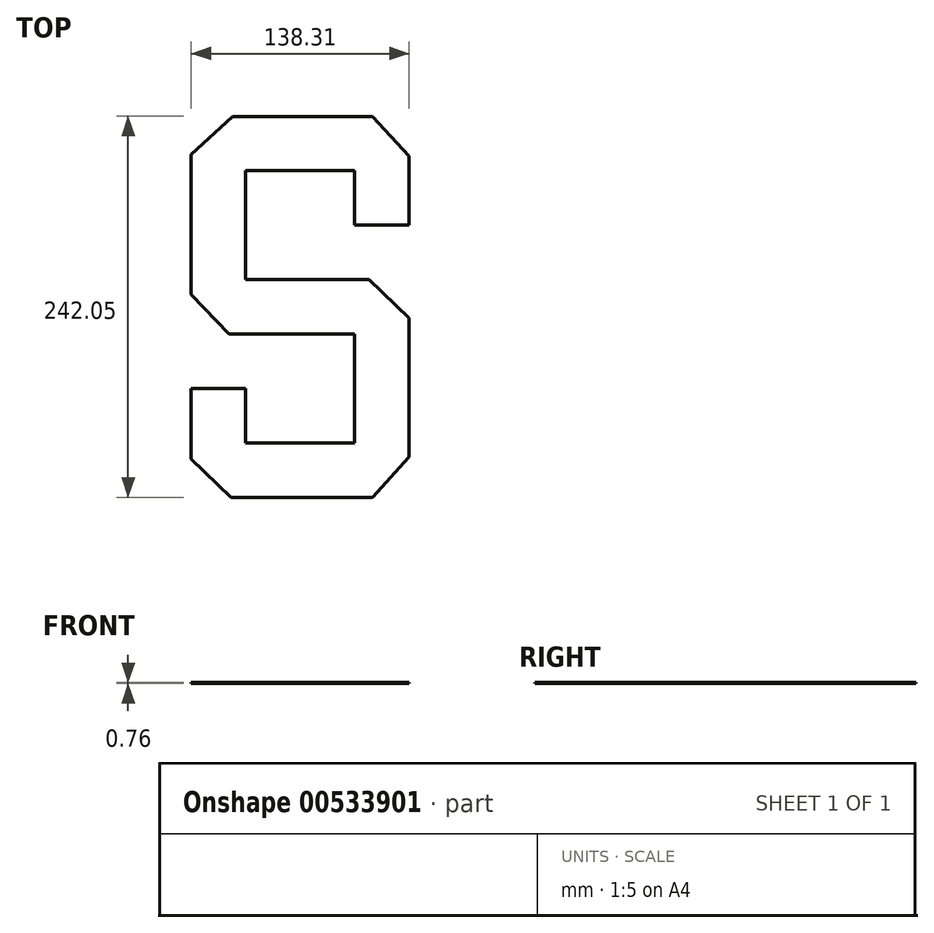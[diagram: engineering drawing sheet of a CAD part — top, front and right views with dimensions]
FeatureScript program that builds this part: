
annotation { "Feature Type Name" : "Feature", "Feature Type Description" : "" }
export const myFeature = defineFeature(function(context is Context, id is Id, definition is map)
    precondition{}
    {
        {
            var Q0;
            Q0=qCreatedBy(makeId("Top.planeOp"),FACE);
            var sketch = newSketch(context, id + "F0", { "sketchPlane" : qUnion([Q0])});
            skLineSegment(sketch, "E0", {"start": v(106.6, 0) * mm, "end": v(106.6, 43.8) * mm});
            skLineSegment(sketch, "E1", {"start": v(83.48, 69.16) * mm, "end": v(-5.42, 69.16) * mm});
            skLineSegment(sketch, "E2", {"start": v(-31.72, 45) * mm, "end": v(-31.72, -43.9) * mm});
            skLineSegment(sketch, "E3", {"start": v(-7.82, -69.16) * mm, "end": v(72.02, -69.16) * mm});
            skLineSegment(sketch, "E4", {"start": v(72.02, -69.16) * mm, "end": v(72.02, -138.31) * mm});
            skLineSegment(sketch, "E5", {"start": v(72.02, -138.31) * mm, "end": v(2.86, -138.31) * mm});
            skLineSegment(sketch, "E6", {"start": v(2.86, -138.31) * mm, "end": v(2.86, -103.74) * mm});
            skLineSegment(sketch, "E7", {"start": v(2.86, -103.74) * mm, "end": v(-31.72, -103.74) * mm});
            skLineSegment(sketch, "E8", {"start": v(-31.72, -103.74) * mm, "end": v(-31.72, -148.42) * mm});
            skLineSegment(sketch, "E9", {"start": v(-6.62, -172.9) * mm, "end": v(83.48, -172.9) * mm});
            skLineSegment(sketch, "E10", {"start": v(106.6, -147.22) * mm, "end": v(106.6, -58.92) * mm});
            skLineSegment(sketch, "E11", {"start": v(81.08, -34.58) * mm, "end": v(2.86, -34.58) * mm});
            skLineSegment(sketch, "E12", {"start": v(2.86, -34.58) * mm, "end": v(2.86, 34.58) * mm});
            skLineSegment(sketch, "E13", {"start": v(2.86, 34.58) * mm, "end": v(72.02, 34.58) * mm});
            skLineSegment(sketch, "E14", {"start": v(72.02, 34.58) * mm, "end": v(72.02, 0) * mm});
            skLineSegment(sketch, "E15", {"start": v(72.02, 0) * mm, "end": v(106.6, 0) * mm});
            skLineSegment(sketch, "E16", {"start": v(83.48, 69.16) * mm, "end": v(106.6, 43.8) * mm});
            skLineSegment(sketch, "E17", {"start": v(-5.42, 69.16) * mm, "end": v(-31.72, 45) * mm});
            skLineSegment(sketch, "E18", {"start": v(-31.72, -43.9) * mm, "end": v(-7.82, -69.16) * mm});
            skLineSegment(sketch, "E19", {"start": v(81.08, -34.58) * mm, "end": v(106.6, -58.92) * mm});
            skLineSegment(sketch, "E20", {"start": v(83.48, -172.9) * mm, "end": v(106.6, -147.22) * mm});
            skPoint(sketch, "E21.end.orphan", {"position": v(0, -172.9) * mm});
            skLineSegment(sketch, "E22", {"start": v(-31.72, -148.42) * mm, "end": v(-6.62, -172.9) * mm});
            skSolve(sketch);
        }
        {
            var Q0;
            Q0 = qSketchRegion(id + "F0", true);
            extrude(context, id + "F1", {"entities" : qUnion([Q0]), "depth" : 0.76 * mm, "offsetDistance" : 25.4 * mm});
        }
    });
